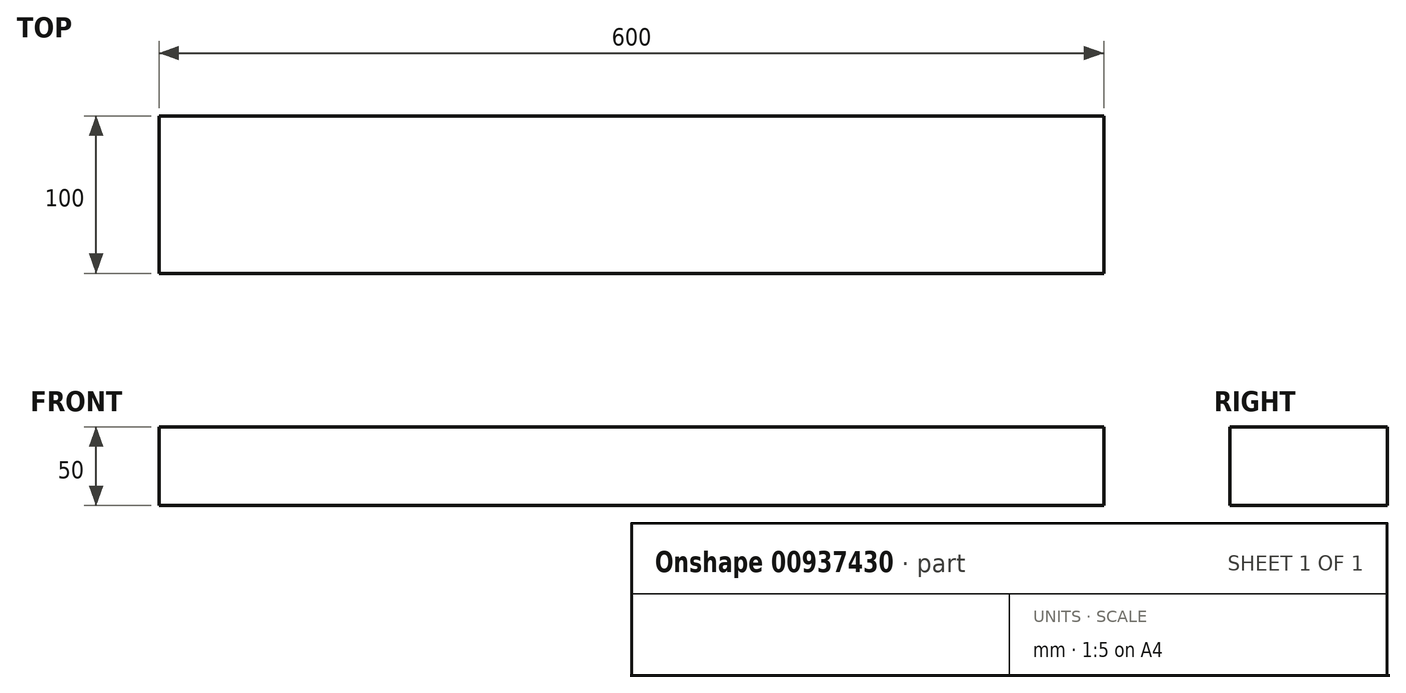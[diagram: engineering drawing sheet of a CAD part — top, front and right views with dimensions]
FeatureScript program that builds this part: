
annotation { "Feature Type Name" : "Feature", "Feature Type Description" : "" }
export const myFeature = defineFeature(function(context is Context, id is Id, definition is map)
    precondition{}
    {
        {
            var Q0;
            Q0=qCreatedBy(makeId("Front.planeOp"),FACE);
            var sketch = newSketch(context, id + "F0", { "sketchPlane" : qUnion([Q0])});
            skLineSegment(sketch, "E0.bottom", {"start": v(-300, 25) * mm, "end": v(300, 25) * mm});
            skLineSegment(sketch, "E0.top", {"start": v(-300, -25) * mm, "end": v(300, -25) * mm});
            skLineSegment(sketch, "E0.left", {"start": v(-300, 25) * mm, "end": v(-300, -25) * mm});
            skLineSegment(sketch, "E0.right", {"start": v(300, 25) * mm, "end": v(300, -25) * mm});
            skPoint(sketch, "E0.middle", {"position": v(0, 0) * mm});
            skPoint(sketch, "E1", {"position": v(400, -25) * mm});
            skCircle(sketch, "E2", {"center": v(400, 0) * mm, "radius": 25 * mm});
            skLineSegment(sketch, "E3.top", {"start": v(-225, 25) * mm, "end": v(-195, 25) * mm});
            skSolve(sketch);
        }
        {
            var Q0;
            Q0 = qSketchRegion(id + "F0", true);
            extrude(context, id + "F1", {"entities" : qUnion([Q0]), "endBound" : BoundingType.SYMMETRIC, "depth" : 100 * mm, "offsetDistance" : 25 * mm});
        }
        {
            var Q0;
            {var subQ0=sQuery(id+"F0.wireOp",EDGE,"E2");var subQ1=makeQuery(id+"F0.imprint","INTERSECT",VERTEX,{"derivedFrom":[sQuery(id+"F0.wireOp",EDGE,"E0.bottom"),subQ0]});Q0=makeQuery(id+"F0.imprint","IMPRINT",FACE,{"disambiguationData":[TD([[makeQuery(id+"F0.imprint","IMPRINT",EDGE,{"disambiguationData":[TD([[subQ1,-1.0]])],"derivedFrom":subQ0}),1.0]])]});}
            extrude(context, id + "F2", {"entities" : qUnion([Q0]), "operationType" : NewBodyOperationType.REMOVE, "endBound" : BoundingType.SYMMETRIC, "oppositeDirection" : true, "depth" : 100 * mm, "offsetDistance" : 25 * mm});
        }
    });
